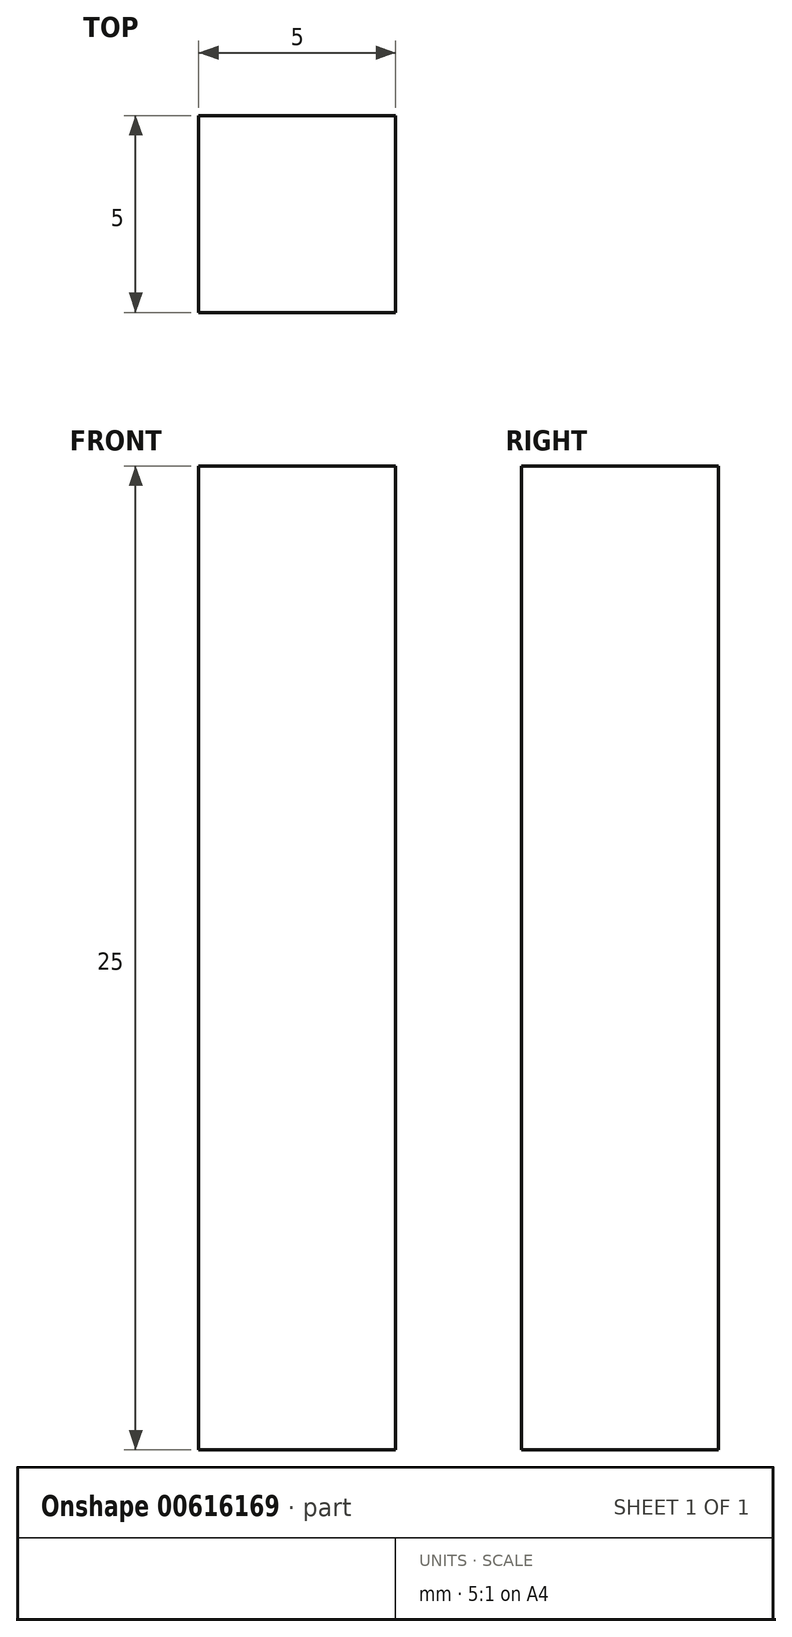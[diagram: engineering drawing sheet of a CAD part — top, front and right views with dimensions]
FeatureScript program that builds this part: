
annotation { "Feature Type Name" : "Feature", "Feature Type Description" : "" }
export const myFeature = defineFeature(function(context is Context, id is Id, definition is map)
    precondition{}
    {
        {
            var Q0;
            Q0=qCreatedBy(makeId("Top.planeOp"),FACE);
            var sketch = newSketch(context, id + "F0", { "sketchPlane" : qUnion([Q0])});
            skLineSegment(sketch, "E0.bottom", {"start": v(-2.5, 2.5) * mm, "end": v(2.5, 2.5) * mm});
            skLineSegment(sketch, "E0.top", {"start": v(-2.5, -2.5) * mm, "end": v(2.5, -2.5) * mm});
            skLineSegment(sketch, "E0.left", {"start": v(-2.5, 2.5) * mm, "end": v(-2.5, -2.5) * mm});
            skLineSegment(sketch, "E0.right", {"start": v(2.5, 2.5) * mm, "end": v(2.5, -2.5) * mm});
            skSolve(sketch);
        }
        {
            var Q0;
            Q0 = qSketchRegion(id + "F0", true);
            extrude(context, id + "F1", {"entities" : qUnion([Q0]), "depth" : 25 * mm, "offsetDistance" : 25 * mm});
        }
    });
